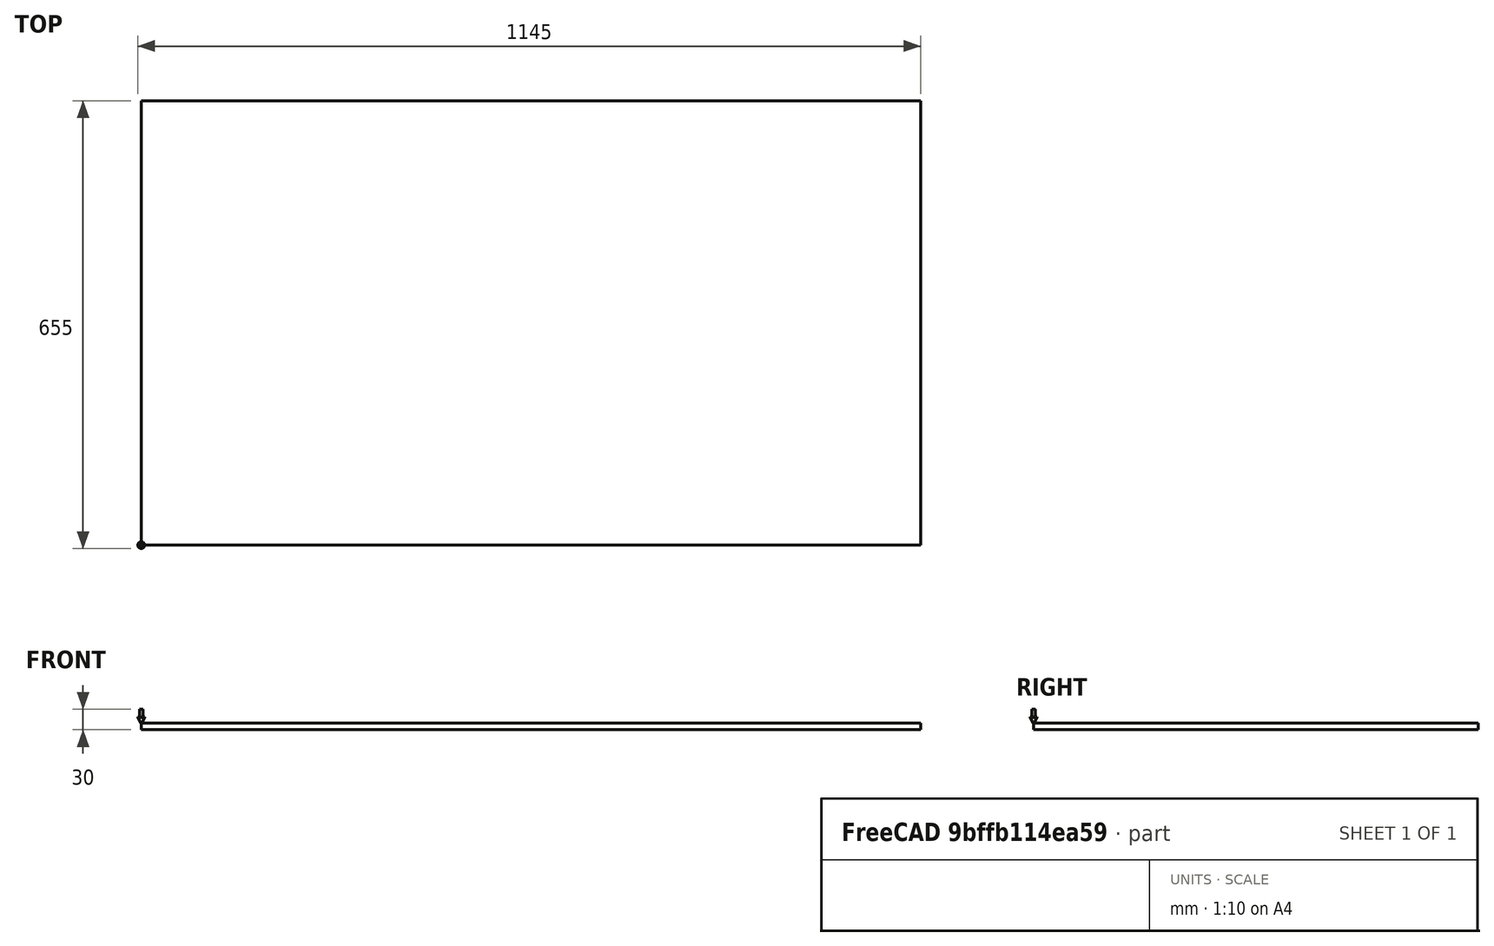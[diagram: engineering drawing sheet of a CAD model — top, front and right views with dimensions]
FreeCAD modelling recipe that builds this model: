
FCSTD DOCUMENT  (FreeCAD 0.19R14555 (Git shallow))
Label: BarrelTable2
License: All rights reserved
LicenseURL: http://en.wikipedia.org/wiki/All_rights_reserved
objects: Part::FeaturePython×3, Path::FeaturePython×3, App::DocumentObjectGroup×2, Sketcher::SketchObject×1, PartDesign::Pad×1, App::FeaturePython×1, PartDesign::Chamfer×1, PartDesign::Body×1, Path::FeatureCompoundPython×1, Mesh::FeaturePython×1
note: 10 computed .brp shape members not serialized (recipe doc carries the construction recipe); baked Part::Feature solids carry a one-line shape summary decoded from their .brp

FEATURE [Sketcher::SketchObject] Sketch
  FullyConstrained = true
  MapMode = 5
  Support = -> [XY_Plane]
  sketch-geometry (5):
    g0: LineSegment StartX=0 StartY=650 StartZ=0 EndX=1140 EndY=650 EndZ=0
    g1: LineSegment StartX=1140 StartY=650 StartZ=0 EndX=1140 EndY=0 EndZ=0
    g2: LineSegment StartX=1140 StartY=0 StartZ=0 EndX=0 EndY=0 EndZ=0
    g3: LineSegment StartX=0 StartY=0 StartZ=0 EndX=0 EndY=650 EndZ=0
    g4: Circle CenterX=570 CenterY=325 CenterZ=0 NormalX=0 NormalY=0 NormalZ=1 AngleXU=0 Radius=307.5
  constraints (14):
    c: Coincident(g0,g1)
    c: Coincident(g1,g2)
    c: Coincident(g2,g3)
    c: Coincident(g3,g0)
    c: Horizontal(g0)
    c: Horizontal(g2)
    c: Vertical(g1)
    c: Vertical(g3)
    c: Coincident(g2,g-1)
    c: DistanceX(g2,g1) = 1140
    c: DistanceY(g2,g0) = 650
    c: DistanceX(g2,g4) = 570
    c: DistanceY(g2,g4) = 325
    c: Diameter(g4) = 615
FEATURE [PartDesign::Pad] Pad
  Direction = (1,1,1)
  Length = 10
  Length2 = 100
  Profile = -> Sketch
  Reversed = true
  Type = 0
FEATURE [App::FeaturePython] SetupSheet  # Path/CAM operation (typed FeaturePython)
  ClearanceHeightExpression = OpStockZMax+SetupSheet.ClearanceHeightOffset
  ClearanceHeightOffset = 5
  CoolantMode = 0
  CoolantModes = None | Flood | Mist
  FinalDepthExpression = OpFinalDepth
  HorizRapid = 0
  SafeHeightExpression = OpStockZMax+SetupSheet.SafeHeightOffset
  SafeHeightOffset = 3
  StartDepthExpression = OpStartDepth
  StepDownExpression = OpToolDiameter
  VertRapid = 0
FEATURE [Part::FeaturePython] Stock001  # WARN: FeaturePython — macro-defined, semantics opaque (R4)
  Height = 10
  Length = 1140
  Placement = pos=(0,0,-10) rot=(0,0,1;0rad)
  StockType = CreateBox
  Width = 650
FEATURE [Part::FeaturePython] ToolBit001  label="60 Deg. V-Bit"  # Path/CAM toolbit (typed FeaturePython)
  BitPropertyNames = Chipload | CuttingEdgeAngle | CuttingEdgeHeight | Diameter | Flutes | Length | Material | ShankDiameter | TipDiameter
  BitShape = /app/freecad/Mod/Path/Tools/Shape/v-bit.fcstd
  Chipload = 0
  CuttingEdgeAngle = 60
  CuttingEdgeHeight = 1
  Diameter = 10
  File = <userpath>/Documents/MensShed/FreeCAD/Bit/60degree_Vbit.fctb
  Flutes = 0
  Length = 20
  Material = 0
  ShankDiameter = 5
  ShapeName = v_bit
  TipDiameter = 1
FEATURE [Path::FeaturePython] _0_Deg__V_Bit  label="60 Deg. V-Bit001"  # Path/CAM operation (typed FeaturePython)
  HorizFeed = 10
  HorizRapid = 0
  SpindleDir = 0
  SpindleSpeed = 10000
  Tool = -> ToolBit001
  ToolNumber = 2
  VertFeed = 10
  VertRapid = 0
  expr: VertRapid = SetupSheet.VertRapid
  expr: HorizRapid = SetupSheet.HorizRapid
FEATURE [App::DocumentObjectGroup] Tools
  Group = -> [_0_Deg__V_Bit]
FEATURE [PartDesign::Chamfer] Chamfer
  Angle = 45
  Base = -> Pad [Edge14]
  BaseFeature = -> Pad
  ChamferType = 0
  FlipDirection = false
  Size = 6
  Size2 = 1
  SupportTransform = false
FEATURE [PartDesign::Body] Body
  Group = -> [Sketch,Pad,Chamfer]
  Origin = -> Origin
  Tip = -> Chamfer
FEATURE [Part::FeaturePython] Clone  label="Model-Body"  # Draft clone (typed FeaturePython)
  AttacherType = Attacher::AttachEngine3D
  Fuse = false
  Objects = -> [Body]
  PathResource = Model
  Scale = (1,1,1)
FEATURE [App::DocumentObjectGroup] Model
  Group = -> [Clone]
FEATURE [Path::FeaturePython] Profile  # Path/CAM operation (typed FeaturePython)
  Active = true
  AreaParams:
    Tolerance = 1e-07
    FitArcs = True
    Simplify = False
    CleanDistance = 0.0
    Accuracy = 0.01
    Unit = 1.0
    MinArcPoints = 4
    MaxArcPoints = 100
    ClipperScale = 10000000.0
    Fill = 0
    Coplanar = 0
    Reorient = True
    Outline = False
    Explode = False
    OpenMode = 0
    Deflection = 0.01
    SubjectFill = 0
    ClipFill = 0
    Offset = -5.0
    ExtraPass = 0
    Stepover = 0.0
    LastStepover = 0.0
    JoinType = 0
    EndType = 0
    MiterLimit = 2.0
    RoundPrecision = 0.0
    PocketMode = 0
    ToolRadius = 1.0
    PocketExtraOffset = 0.0
    PocketStepover = 0.0
    PocketLastStepover = 0.0
    FromCenter = False
    Angle = 45.0
    AngleShift = 0.0
    Shift = 0.0
    Thicken = False
    SectionCount = -1
    Stepdown = 1.0
    SectionOffset = 0.0
    SectionTolerance = 1e-06
    SectionMode = 2
    Project = False
  AttemptInverseAngle = true
  Base = -> [Clone]
  ClearanceHeight = 5
  CoolantMode = None
  CycleTime = 00:07:31
  Direction = 0
  EnableRotation = 0
  FinalDepth = -6
  HandleMultipleFeatures = 0
  InverseAngle = false
  JoinType = 0
  LimitDepthToFace = true
  MiterLimit = 0.1
  OffsetExtra = 0
  OpFinalDepth = -6
  OpStartDepth = 0
  OpStockZMax = 0
  OpStockZMin = -10
  OpToolDiameter = 10
  PathParams = {'orientation': 1, 'feedrate': 10.0, 'feedrate_v': 10.0, 'verbose': True, 'resume_height': 3.0, 'retraction': 5.0, 'return_end': True, 'preamble': False}
  ReverseDirection = false
  SafeHeight = 3
  Side = 1
  StartDepth = 0
  StartPoint = (0,0,0)
  StepDown = 2
  ToolController = -> _0_Deg__V_Bit
  UseComp = true
  UseStartPoint = false
  processCircles = false
  processHoles = false
  processPerimeter = true
  expr: StartDepth = OpStartDepth
  expr: FinalDepth = OpFinalDepth
  expr: StepDown = 2
  expr: SafeHeight = OpStockZMax + SetupSheet.SafeHeightOffset
  expr: ClearanceHeight = OpStockZMax + SetupSheet.ClearanceHeightOffset
FEATURE [Path::FeatureCompoundPython] Operations  # Path/CAM operation (typed FeaturePython)
  Group = -> [Profile]
  UsePlacements = false
FEATURE [Path::FeaturePython] Job  # Path/CAM operation (typed FeaturePython)
  CycleTime = 00:07:31
  Fixtures = G54
  GeometryTolerance = 0.01
  LastPostProcessDate = 2022-01-20 11:16:55.277447
  LastPostProcessOutput = <userpath>/Documents/MensShed/BarrelTable2.ngc
  Model = -> Model
  Operations = -> Operations
  OrderOutputBy = 0
  PostProcessor = 7
  PostProcessorOutputFile = <userpath>/Documents/MensShed/BarrelTable2.ngc
  SetupSheet = -> SetupSheet
  SplitOutput = false
  Stock = -> Stock001
  Tools = -> Tools
FEATURE [Mesh::FeaturePython] CutMaterial  # WARN: FeaturePython — macro-defined, semantics opaque (R4)
